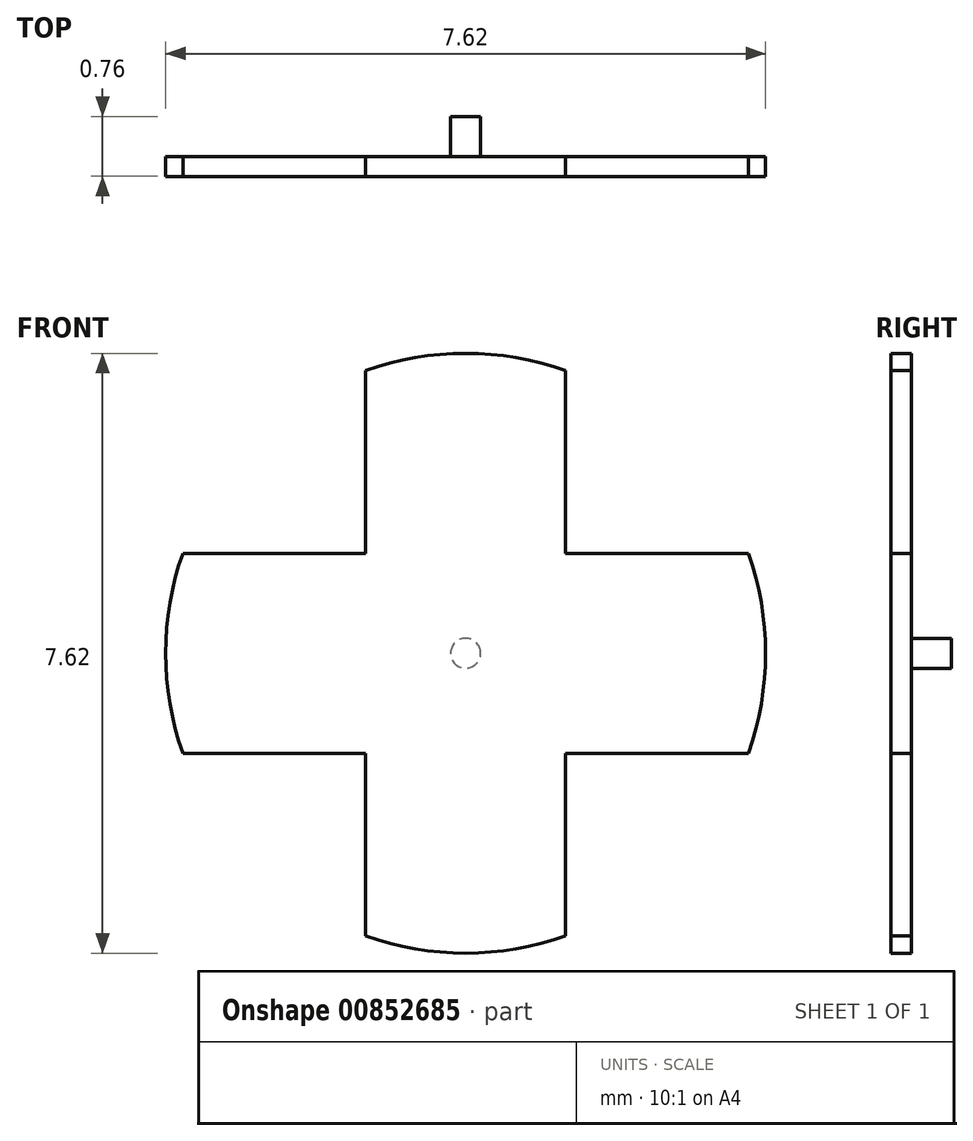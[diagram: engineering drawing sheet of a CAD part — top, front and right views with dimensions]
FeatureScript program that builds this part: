
annotation { "Feature Type Name" : "Feature", "Feature Type Description" : "" }
export const myFeature = defineFeature(function(context is Context, id is Id, definition is map)
    precondition{}
    {
        {
            var Q0;
            Q0=qCreatedBy(makeId("Front.planeOp"),FACE);
            var sketch = newSketch(context, id + "F0", { "sketchPlane" : qUnion([Q0])});
            skArc(sketch, "E0", {"start": v(-3.6, 1.27) * mm, "mid": v(-3.81, 0) * mm, "end": v(-3.6, -1.27) * mm});
            skLineSegment(sketch, "E1.left", {"start": v(-1.27, 3.6) * mm, "end": v(-1.27, 1.27) * mm});
            skLineSegment(sketch, "E1.right", {"start": v(1.27, 3.6) * mm, "end": v(1.27, 1.27) * mm});
            skLineSegment(sketch, "E2.bottom", {"start": v(-3.6, 1.27) * mm, "end": v(-1.27, 1.27) * mm});
            skLineSegment(sketch, "E2.top", {"start": v(-3.6, -1.27) * mm, "end": v(-1.27, -1.27) * mm});
            skArc(sketch, "E3.trimOffspring", {"start": v(1.27, 3.6) * mm, "mid": v(0, 3.81) * mm, "end": v(-1.27, 3.6) * mm});
            skArc(sketch, "E4.trimOffspring", {"start": v(3.6, -1.27) * mm, "mid": v(3.81, 0) * mm, "end": v(3.6, 1.27) * mm});
            skArc(sketch, "E5.trimOffspring", {"start": v(-1.27, -3.6) * mm, "mid": v(0, -3.81) * mm, "end": v(1.27, -3.6) * mm});
            skPoint(sketch, "E2.left.end.orphan", {"position": v(-6.54, -1.27) * mm});
            skPoint(sketch, "E6.orphan", {"position": v(-6.54, 1.27) * mm});
            skPoint(sketch, "E1.bottom.start.orphan", {"position": v(-1.27, 4.91) * mm});
            skPoint(sketch, "E7.orphan", {"position": v(1.27, 4.91) * mm});
            skPoint(sketch, "E2.right.start.orphan", {"position": v(6.54, 1.27) * mm});
            skPoint(sketch, "E8.orphan", {"position": v(6.54, -1.27) * mm});
            skPoint(sketch, "E1.top.start.orphan", {"position": v(-1.27, -4.91) * mm});
            skPoint(sketch, "E9.orphan", {"position": v(1.27, -4.91) * mm});
            skLineSegment(sketch, "E10.trimOffspring", {"start": v(-1.27, -1.27) * mm, "end": v(-1.27, -3.6) * mm});
            skLineSegment(sketch, "E11.trimOffspring", {"start": v(1.27, 1.27) * mm, "end": v(3.6, 1.27) * mm});
            skLineSegment(sketch, "E12.trimOffspring", {"start": v(1.27, -1.27) * mm, "end": v(1.27, -3.6) * mm});
            skLineSegment(sketch, "E13.trimOffspring", {"start": v(1.27, -1.27) * mm, "end": v(3.6, -1.27) * mm});
            skCircle(sketch, "E14", {"center": v(0, 0) * mm, "radius": 0.2 * mm});
            skSolve(sketch);
        }
        {
            var Q0;
            Q0=makeQuery(id+"F0.imprint","IMPRINT",FACE,{"disambiguationData":[TD([[makeQuery(id+"F0.imprint","IMPRINT",EDGE,{"derivedFrom":sQuery(id+"F0.wireOp",EDGE,"E0")}),1.0]])]});
            var Q1;
            Q1=makeQuery(id+"F0.imprint","IMPRINT",FACE,{"disambiguationData":[TD([[makeQuery(id+"F0.imprint","IMPRINT",EDGE,{"derivedFrom":sQuery(id+"F0.wireOp",EDGE,"E14")}),1.0]])]});
            extrude(context, id + "F1", {"entities" : qUnion([Q0, Q1]), "depth" : 0.25 * mm, "offsetDistance" : 25.4 * mm});
        }
        {
            var Q0;
            Q0=makeQuery(id+"F0.imprint","IMPRINT",FACE,{"disambiguationData":[TD([[makeQuery(id+"F0.imprint","IMPRINT",EDGE,{"derivedFrom":sQuery(id+"F0.wireOp",EDGE,"E14")}),1.0]])]});
            extrude(context, id + "F2", {"entities" : qUnion([Q0]), "operationType" : NewBodyOperationType.ADD, "oppositeDirection" : true, "depth" : 0.5 * mm, "offsetDistance" : 25.4 * mm});
        }
    });
